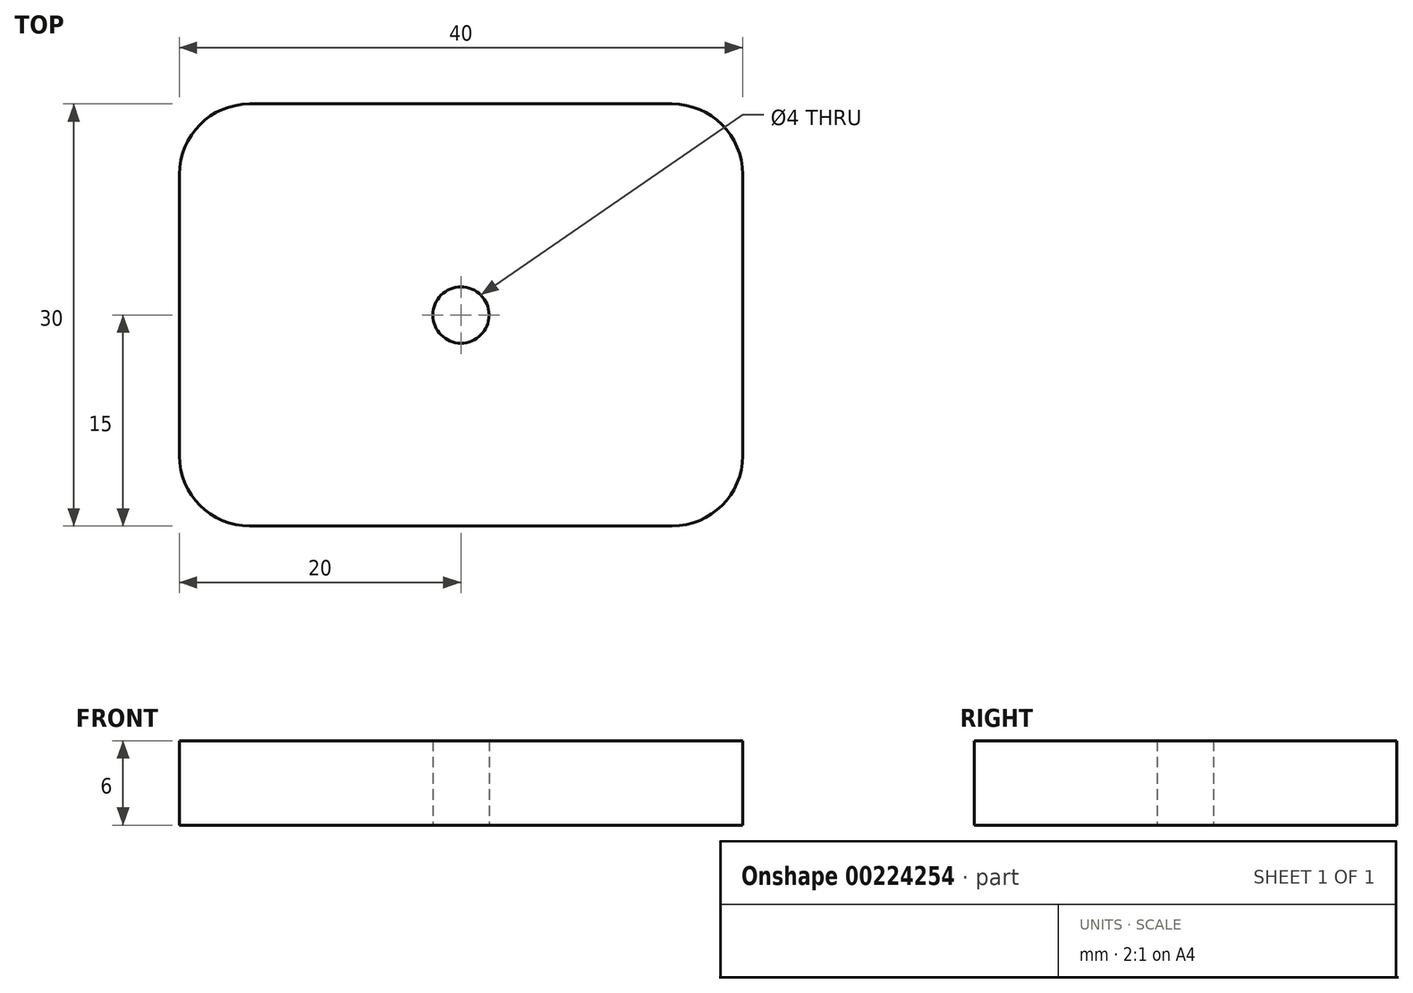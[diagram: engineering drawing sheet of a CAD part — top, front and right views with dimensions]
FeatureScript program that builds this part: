
annotation { "Feature Type Name" : "Feature", "Feature Type Description" : "" }
export const myFeature = defineFeature(function(context is Context, id is Id, definition is map)
    precondition{}
    {
        {
            var Q0;
            Q0=qCreatedBy(makeId("Top.planeOp"),FACE);
            var sketch = newSketch(context, id + "F2", { "sketchPlane" : qUnion([Q0])});
            skLineSegment(sketch, "E0.bottom", {"start": v(0, 0) * mm, "end": v(40, 0) * mm});
            skLineSegment(sketch, "E0.top", {"start": v(0, 30) * mm, "end": v(40, 30) * mm});
            skLineSegment(sketch, "E0.left", {"start": v(0, 0) * mm, "end": v(0, 30) * mm});
            skLineSegment(sketch, "E0.right", {"start": v(40, 0) * mm, "end": v(40, 30) * mm});
            skCircle(sketch, "E1", {"center": v(20, 15) * mm, "radius": 2 * mm});
            skPoint(sketch, "E1.centerSnap0", {"position": v(40, 15) * mm});
            skPoint(sketch, "E1.centerSnap1", {"position": v(20, 30) * mm});
            skSolve(sketch);
        }
        {
            var Q0;
            Q0=makeQuery(id+"F2.imprint","IMPRINT",FACE,{"disambiguationData":[TD([[makeQuery(id+"F2.imprint","IMPRINT",EDGE,{"derivedFrom":sQuery(id+"F2.wireOp",EDGE,"E0.bottom")}),1.0]])]});
            extrude(context, id + "F0", {"entities" : qUnion([Q0]), "depth" : 6 * mm});
        }
        {
            var Q0;
            Q0=makeQuery(id+"F0.opExtrude","SWEPT_EDGE",EDGE,{"disambiguationData":[OSD([sQuery(id+"F2.wireOp",EDGE,"E0.top"),sQuery(id+"F2.wireOp",EDGE,"E0.left")])]});
            var Q1;
            Q1=makeQuery(id+"F0.opExtrude","SWEPT_EDGE",EDGE,{"disambiguationData":[OSD([sQuery(id+"F2.wireOp",EDGE,"E0.top"),sQuery(id+"F2.wireOp",EDGE,"E0.right")])]});
            var Q2;
            Q2=makeQuery(id+"F0.opExtrude","SWEPT_EDGE",EDGE,{"disambiguationData":[OSD([sQuery(id+"F2.wireOp",EDGE,"E0.bottom"),sQuery(id+"F2.wireOp",EDGE,"E0.right")])]});
            var Q3;
            Q3=makeQuery(id+"F0.opExtrude","SWEPT_EDGE",EDGE,{"disambiguationData":[OSD([sQuery(id+"F2.wireOp",EDGE,"E0.bottom"),sQuery(id+"F2.wireOp",EDGE,"E0.left")])]});
            fillet(context, id + "F1", {"entities" : qUnion([Q0, Q1, Q2, Q3]), "radius" : 5 * mm, "tangentPropagation" : true, "allowEdgeOverflow" : false});
        }
    });
